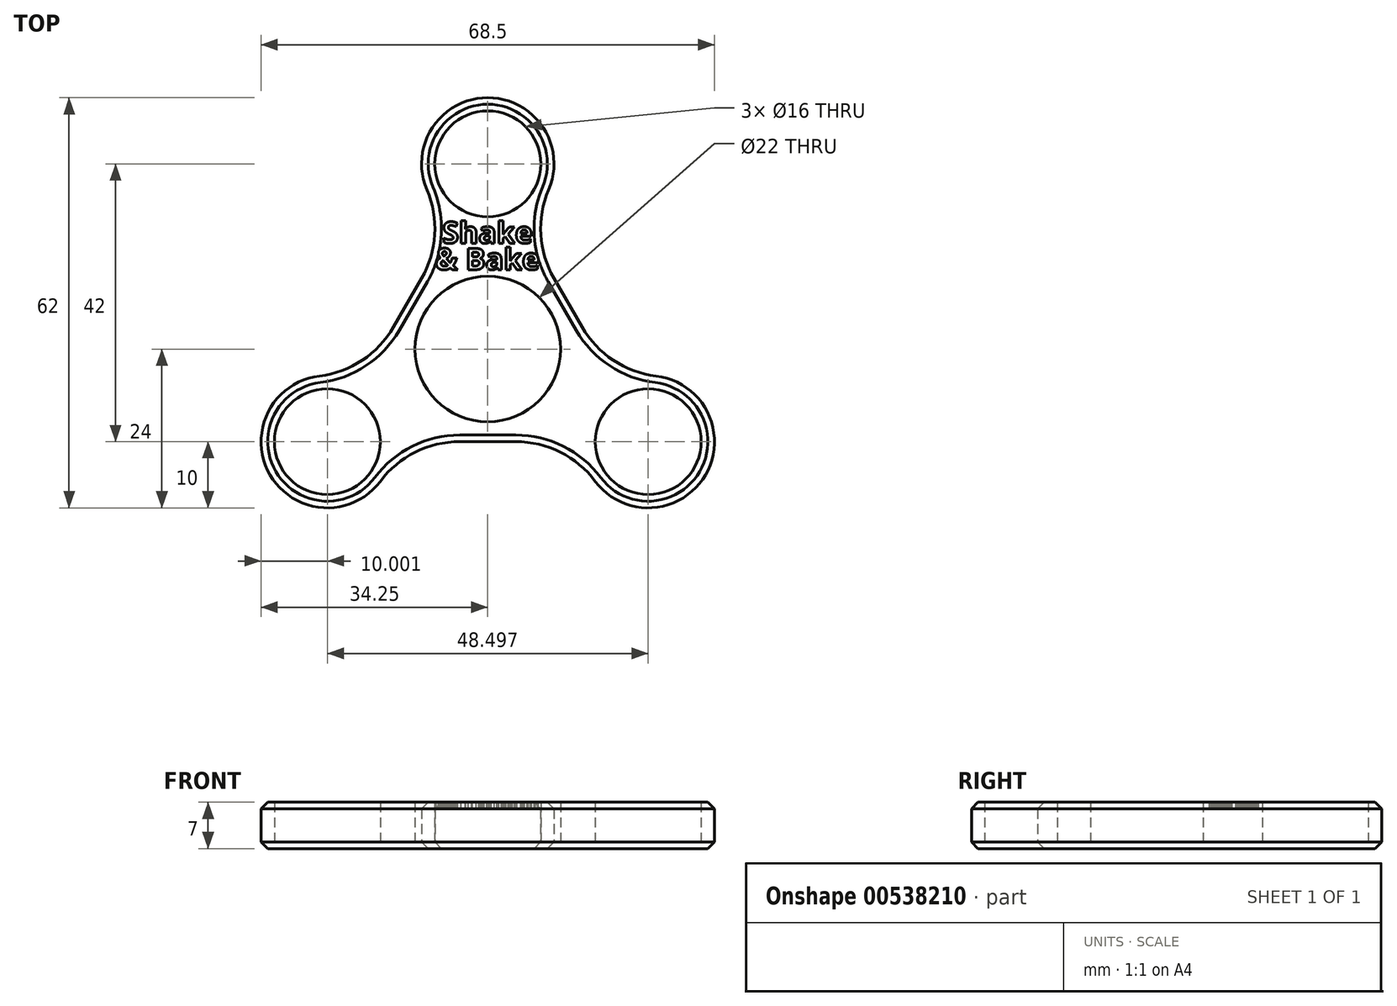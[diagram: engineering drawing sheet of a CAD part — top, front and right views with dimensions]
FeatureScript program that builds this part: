
annotation { "Feature Type Name" : "Feature", "Feature Type Description" : "" }
export const myFeature = defineFeature(function(context is Context, id is Id, definition is map)
    precondition{}
    {
        {
            var Q0;
            Q0=qCreatedBy(makeId("Top.planeOp"),FACE);
            var sketch = newSketch(context, id + "F0", { "sketchPlane" : qUnion([Q0])});
            skCircle(sketch, "E0.cCircle", {"center": v(0, 0) * mm, "radius": 28 * mm, "construction": true});
            skLineSegment(sketch, "E0.0", {"start": v(0, 28) * mm, "end": v(24.25, -14) * mm});
            skLineSegment(sketch, "E0.1", {"start": v(24.25, -14) * mm, "end": v(-24.25, -14) * mm});
            skLineSegment(sketch, "E0.2", {"start": v(-24.25, -14) * mm, "end": v(0, 28) * mm});
            skCircle(sketch, "E1", {"center": v(0, 0) * mm, "radius": 11 * mm});
            skCircle(sketch, "E2", {"center": v(0, 28) * mm, "radius": 8 * mm});
            skCircle(sketch, "E3", {"center": v(24.25, -14) * mm, "radius": 8 * mm});
            skCircle(sketch, "E4", {"center": v(-24.25, -14) * mm, "radius": 8 * mm});
            skCircle(sketch, "E5", {"center": v(0, 28) * mm, "radius": 10 * mm});
            skCircle(sketch, "E6", {"center": v(24.25, -14) * mm, "radius": 10 * mm});
            skCircle(sketch, "E7", {"center": v(-24.25, -14) * mm, "radius": 10 * mm});
            skSolve(sketch);
        }
        {
            var Q0;
            {var subQ0=sQuery(id+"F0.wireOp",EDGE,"E5");var subQ1=sQuery(id+"F0.wireOp",EDGE,"E0.0");var subQ2=makeQuery(id+"F0.imprint","INTERSECT",VERTEX,{"derivedFrom":[subQ1,subQ0]});Q0=makeQuery(id+"F0.imprint","IMPRINT",FACE,{"disambiguationData":[TD([[makeQuery(id+"F0.imprint","IMPRINT",EDGE,{"disambiguationData":[TD([[subQ2,1.0]])],"derivedFrom":subQ1}),1.0]])]});}
            var Q1;
            Q1=makeQuery(id+"F0.imprint","IMPRINT",FACE,{"disambiguationData":[TD([[makeQuery(id+"F0.imprint","IMPRINT",EDGE,{"derivedFrom":sQuery(id+"F0.wireOp",EDGE,"E1")}),-1.0]])]});
            var Q2;
            {var subQ0=sQuery(id+"F0.wireOp",EDGE,"E5");var subQ1=sQuery(id+"F0.wireOp",EDGE,"E0.0");var subQ2=makeQuery(id+"F0.imprint","INTERSECT",VERTEX,{"derivedFrom":[subQ1,subQ0]});Q2=makeQuery(id+"F0.imprint","IMPRINT",FACE,{"disambiguationData":[TD([[makeQuery(id+"F0.imprint","IMPRINT",EDGE,{"disambiguationData":[TD([[subQ2,1.0]])],"derivedFrom":subQ1}),-1.0]])]});}
            var Q3;
            {var subQ0=sQuery(id+"F0.wireOp",EDGE,"E7");var subQ1=sQuery(id+"F0.wireOp",EDGE,"E0.1");var subQ2=makeQuery(id+"F0.imprint","INTERSECT",VERTEX,{"derivedFrom":[subQ1,subQ0]});Q3=makeQuery(id+"F0.imprint","IMPRINT",FACE,{"disambiguationData":[TD([[makeQuery(id+"F0.imprint","IMPRINT",EDGE,{"disambiguationData":[TD([[subQ2,-1.0]])],"derivedFrom":subQ1}),1.0]])]});}
            var Q4;
            {var subQ0=sQuery(id+"F0.wireOp",EDGE,"E7");var subQ1=sQuery(id+"F0.wireOp",EDGE,"E0.1");var subQ2=makeQuery(id+"F0.imprint","INTERSECT",VERTEX,{"derivedFrom":[subQ1,subQ0]});Q4=makeQuery(id+"F0.imprint","IMPRINT",FACE,{"disambiguationData":[TD([[makeQuery(id+"F0.imprint","IMPRINT",EDGE,{"disambiguationData":[TD([[subQ2,-1.0]])],"derivedFrom":subQ1}),-1.0]])]});}
            var Q5;
            {var subQ0=sQuery(id+"F0.wireOp",EDGE,"E6");var subQ1=sQuery(id+"F0.wireOp",EDGE,"E0.0");var subQ2=makeQuery(id+"F0.imprint","INTERSECT",VERTEX,{"derivedFrom":[subQ1,subQ0]});Q5=makeQuery(id+"F0.imprint","IMPRINT",FACE,{"disambiguationData":[TD([[makeQuery(id+"F0.imprint","IMPRINT",EDGE,{"disambiguationData":[TD([[subQ2,-1.0]])],"derivedFrom":subQ1}),-1.0]])]});}
            var Q6;
            {var subQ0=sQuery(id+"F0.wireOp",EDGE,"E6");var subQ1=sQuery(id+"F0.wireOp",EDGE,"E0.0");var subQ2=makeQuery(id+"F0.imprint","INTERSECT",VERTEX,{"derivedFrom":[subQ1,subQ0]});Q6=makeQuery(id+"F0.imprint","IMPRINT",FACE,{"disambiguationData":[TD([[makeQuery(id+"F0.imprint","IMPRINT",EDGE,{"disambiguationData":[TD([[subQ2,-1.0]])],"derivedFrom":subQ1}),1.0]])]});}
            extrude(context, id + "F1", {"entities" : qUnion([Q0, Q1, Q2, Q3, Q4, Q5, Q6]), "depth" : 7 * mm});
        }
        {
            var Q0;
            Q0=makeQuery(id+"F1.opExtrude","SWEPT_EDGE",EDGE,{"disambiguationData":[OSD([sQuery(id+"F0.wireOp",EDGE,"E0.1"),sQuery(id+"F0.wireOp",EDGE,"E6")])]});
            var Q1;
            Q1=makeQuery(id+"F1.opExtrude","SWEPT_EDGE",EDGE,{"disambiguationData":[OSD([sQuery(id+"F0.wireOp",EDGE,"E0.1"),sQuery(id+"F0.wireOp",EDGE,"E7")])]});
            var Q2;
            Q2=makeQuery(id+"F1.opExtrude","SWEPT_EDGE",EDGE,{"disambiguationData":[OSD([sQuery(id+"F0.wireOp",EDGE,"E0.2"),sQuery(id+"F0.wireOp",EDGE,"E7")])]});
            var Q3;
            Q3=makeQuery(id+"F1.opExtrude","SWEPT_EDGE",EDGE,{"disambiguationData":[OSD([sQuery(id+"F0.wireOp",EDGE,"E0.0"),sQuery(id+"F0.wireOp",EDGE,"E5")])]});
            var Q4;
            Q4=makeQuery(id+"F1.opExtrude","SWEPT_EDGE",EDGE,{"disambiguationData":[OSD([sQuery(id+"F0.wireOp",EDGE,"E0.2"),sQuery(id+"F0.wireOp",EDGE,"E5")])]});
            var Q5;
            Q5=makeQuery(id+"F1.opExtrude","SWEPT_EDGE",EDGE,{"disambiguationData":[OSD([sQuery(id+"F0.wireOp",EDGE,"E0.0"),sQuery(id+"F0.wireOp",EDGE,"E6")])]});
            fillet(context, id + "F2", {"entities" : qUnion([Q0, Q1, Q2, Q3, Q4, Q5]), "radius" : 15 * mm, "tangentPropagation" : true, "allowEdgeOverflow" : false});
        }
        {
            var Q0;
            {var subQ0=sQuery(id+"F0.wireOp",EDGE,"E7");var subQ1=sQuery(id+"F0.wireOp",EDGE,"E0.1");Q0=makeQuery(id+"F2.opFillet","BLEND_EDGE",EDGE,{"blendedFrom":[makeQuery(id+"F1.opExtrude","SWEPT_EDGE",EDGE,{"disambiguationData":[OSD([subQ1,subQ0])]}),makeQuery(id+"F1.opExtrude","CAP_FACE",FACE,{"disambiguationData":[OSD([sQuery(id+"F0.wireOp",EDGE,"E0.0"),subQ1,sQuery(id+"F0.wireOp",EDGE,"E0.2"),sQuery(id+"F0.wireOp",EDGE,"E1"),sQuery(id+"F0.wireOp",EDGE,"E2"),sQuery(id+"F0.wireOp",EDGE,"E3"),sQuery(id+"F0.wireOp",EDGE,"E4"),sQuery(id+"F0.wireOp",EDGE,"E5"),sQuery(id+"F0.wireOp",EDGE,"E6"),subQ0])],"isStart":false})],"blendedInto":[makeQuery(id+"F1.opExtrude","CAP_FACE",FACE,{"disambiguationData":[OSD([sQuery(id+"F0.wireOp",EDGE,"E0.0"),subQ1,sQuery(id+"F0.wireOp",EDGE,"E0.2"),sQuery(id+"F0.wireOp",EDGE,"E1"),sQuery(id+"F0.wireOp",EDGE,"E2"),sQuery(id+"F0.wireOp",EDGE,"E3"),sQuery(id+"F0.wireOp",EDGE,"E4"),sQuery(id+"F0.wireOp",EDGE,"E5"),sQuery(id+"F0.wireOp",EDGE,"E6"),subQ0])],"isStart":false})]});}
            var Q1;
            {var subQ0=sQuery(id+"F0.wireOp",EDGE,"E7");var subQ1=sQuery(id+"F0.wireOp",EDGE,"E0.1");Q1=makeQuery(id+"F2.opFillet","BLEND_EDGE",EDGE,{"blendedFrom":[makeQuery(id+"F1.opExtrude","SWEPT_EDGE",EDGE,{"disambiguationData":[OSD([subQ1,subQ0])]}),makeQuery(id+"F1.opExtrude","CAP_FACE",FACE,{"disambiguationData":[OSD([sQuery(id+"F0.wireOp",EDGE,"E0.0"),subQ1,sQuery(id+"F0.wireOp",EDGE,"E0.2"),sQuery(id+"F0.wireOp",EDGE,"E1"),sQuery(id+"F0.wireOp",EDGE,"E2"),sQuery(id+"F0.wireOp",EDGE,"E3"),sQuery(id+"F0.wireOp",EDGE,"E4"),sQuery(id+"F0.wireOp",EDGE,"E5"),sQuery(id+"F0.wireOp",EDGE,"E6"),subQ0])],"isStart":true})],"blendedInto":[makeQuery(id+"F1.opExtrude","CAP_FACE",FACE,{"disambiguationData":[OSD([sQuery(id+"F0.wireOp",EDGE,"E0.0"),subQ1,sQuery(id+"F0.wireOp",EDGE,"E0.2"),sQuery(id+"F0.wireOp",EDGE,"E1"),sQuery(id+"F0.wireOp",EDGE,"E2"),sQuery(id+"F0.wireOp",EDGE,"E3"),sQuery(id+"F0.wireOp",EDGE,"E4"),sQuery(id+"F0.wireOp",EDGE,"E5"),sQuery(id+"F0.wireOp",EDGE,"E6"),subQ0])],"isStart":true})]});}
            chamfer(context, id + "F3", {"entities" : qUnion([Q0, Q1]), "width" : 1 * mm, "tangentPropagation" : true});
        }
        {
            var Q0;
            Q0=makeQuery(id+"F1.opExtrude","CAP_FACE",FACE,{"disambiguationData":[OSD([sQuery(id+"F0.wireOp",EDGE,"E0.0"),sQuery(id+"F0.wireOp",EDGE,"E0.1"),sQuery(id+"F0.wireOp",EDGE,"E0.2"),sQuery(id+"F0.wireOp",EDGE,"E1"),sQuery(id+"F0.wireOp",EDGE,"E2"),sQuery(id+"F0.wireOp",EDGE,"E3"),sQuery(id+"F0.wireOp",EDGE,"E4"),sQuery(id+"F0.wireOp",EDGE,"E5"),sQuery(id+"F0.wireOp",EDGE,"E6"),sQuery(id+"F0.wireOp",EDGE,"E7")])],"isStart":false});
            var sketch = newSketch(context, id + "F4", { "sketchPlane" : qUnion([Q0])});
            skText(sketch, "E8", { "text": "Shake", "fontName": "OpenSans-Bold.ttf"});
            skText(sketch, "E9", { "text": "& Bake", "fontName": "OpenSans-Bold.ttf"});
            const initialGuessF4  = {"E8": [-0.00687, 0.016, 1, 0, 0.00325], "E9": [-0.00794, 0.012, 1, 0, 0.00325]};
            skSetInitialGuess(sketch, initialGuessF4);
            skSolve(sketch);
        }
        {
            var Q0;
            Q0=qSketchRegion(id+"F4",true);
            extrude(context, id + "F5", {"entities" : qUnion([Q0]), "operationType" : NewBodyOperationType.REMOVE, "oppositeDirection" : true, "depth" : 1 * mm});
        }
    });
